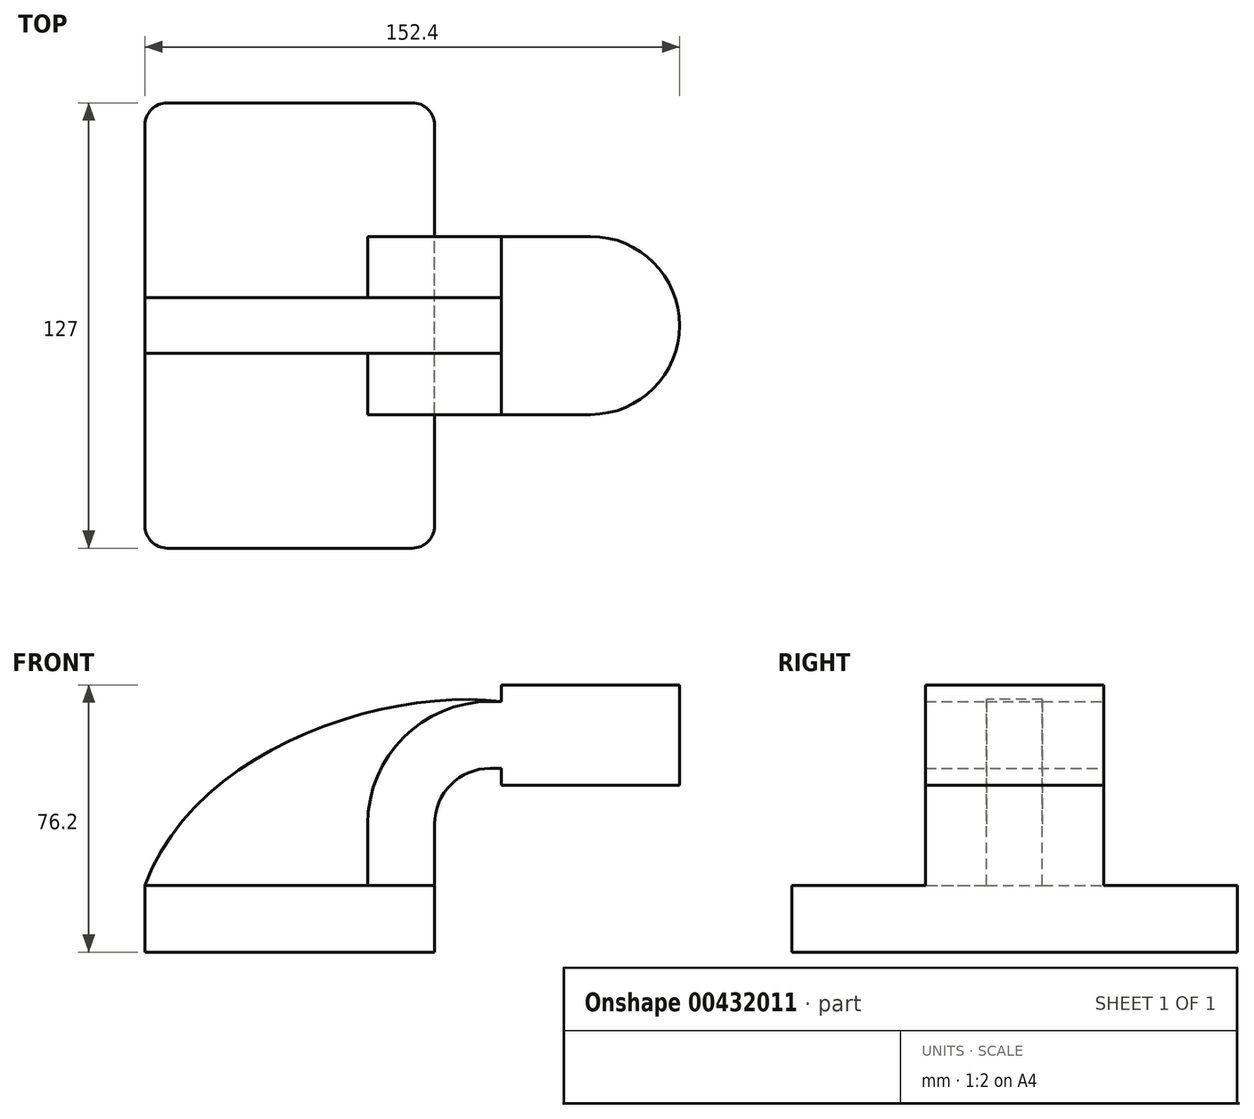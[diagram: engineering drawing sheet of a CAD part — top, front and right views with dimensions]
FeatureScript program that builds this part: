
annotation { "Feature Type Name" : "Feature", "Feature Type Description" : "" }
export const myFeature = defineFeature(function(context is Context, id is Id, definition is map)
    precondition{}
    {
        {
            var Q0;
            Q0=qCreatedBy(makeId("Front.planeOp"),FACE);
            var sketch = newSketch(context, id + "F0", { "sketchPlane" : qUnion([Q0])});
            skLineSegment(sketch, "E0.bottom", {"start": v(-41.28, -9.53) * mm, "end": v(41.28, -9.53) * mm});
            skLineSegment(sketch, "E0.top", {"start": v(-41.28, 9.53) * mm, "end": v(41.28, 9.53) * mm});
            skLineSegment(sketch, "E0.left", {"start": v(-41.28, -9.53) * mm, "end": v(-41.28, 9.53) * mm});
            skLineSegment(sketch, "E0.right", {"start": v(41.28, -9.53) * mm, "end": v(41.28, 9.53) * mm});
            skPoint(sketch, "E0.middle", {"position": v(0, 0) * mm});
            skLineSegment(sketch, "E1.bottom", {"start": v(111.12, 38.1) * mm, "end": v(60.32, 38.1) * mm});
            skLineSegment(sketch, "E1.top", {"start": v(111.13, 66.67) * mm, "end": v(60.33, 66.67) * mm});
            skLineSegment(sketch, "E1.left", {"start": v(111.13, 38.1) * mm, "end": v(111.13, 66.67) * mm});
            skLineSegment(sketch, "E1.right", {"start": v(60.33, 38.1) * mm, "end": v(60.33, 66.68) * mm});
            skPoint(sketch, "E1.middle", {"position": v(85.73, 52.39) * mm});
            skLineSegment(sketch, "E2", {"start": v(41.28, 9.52) * mm, "end": v(41.28, 27) * mm});
            skArc(sketch, "E3", {"start": v(41.27, 27) * mm, "mid": v(45.92, 38.23) * mm, "end": v(57.15, 42.88) * mm});
            skLineSegment(sketch, "E4", {"start": v(57.15, 42.88) * mm, "end": v(60.33, 42.88) * mm});
            skLineSegment(sketch, "E5.0", {"start": v(57.15, 61.93) * mm, "end": v(60.33, 61.93) * mm});
            skArc(sketch, "E5.1", {"start": v(22.23, 27) * mm, "mid": v(32.45, 51.7) * mm, "end": v(57.15, 61.93) * mm});
            skLineSegment(sketch, "E5.2", {"start": v(22.22, 9.52) * mm, "end": v(22.22, 27) * mm});
            skLineSegment(sketch, "E6", {"start": v(85.72, 38.1) * mm, "end": v(85.73, 66.67) * mm});
            skFitSpline(sketch, "E7", {"points": [v(-41.28, 9.53) * mm, v(60.33, 61.93) * mm], "startDerivative": vector(42.58, 116.43) * mm, "endDerivative": vector(100.86, -12.26) * mm});
            skSolve(sketch);
        }
        {
            var Q0;
            Q0=makeQuery(id+"F0.imprint","IMPRINT",FACE,{"disambiguationData":[TD([[makeQuery(id+"F0.imprint","IMPRINT",EDGE,{"derivedFrom":sQuery(id+"F0.wireOp",EDGE,"E0.bottom")}),1.0]])]});
            extrude(context, id + "F1", {"entities" : qUnion([Q0]), "endBound" : BoundingType.SYMMETRIC, "depth" : 127 * mm});
        }
        {
            var Q0;
            {var subQ0=sQuery(id+"F0.wireOp",EDGE,"E2");Q0=makeQuery(id+"F0.imprint","IMPRINT",FACE,{"disambiguationData":[TD([[makeQuery(id+"F0.imprint","IMPRINT",EDGE,{"derivedFrom":subQ0}),1.0]])]});}
            var Q1;
            {var subQ6=sQuery(id+"F0.wireOp",EDGE,"E6");Q1=makeQuery(id+"F0.imprint","IMPRINT",FACE,{"disambiguationData":[TD([[makeQuery(id+"F0.imprint","IMPRINT",EDGE,{"derivedFrom":subQ6}),1.0]])]});}
            extrude(context, id + "F2", {"entities" : qUnion([Q0, Q1]), "operationType" : NewBodyOperationType.ADD, "endBound" : BoundingType.SYMMETRIC, "depth" : 50.8 * mm});
        }
        {
            var Q0;
            Q0=makeQuery(id+"F0.imprint","IMPRINT",FACE,{"disambiguationData":[TD([[makeQuery(id+"F0.imprint","IMPRINT",EDGE,{"derivedFrom":sQuery(id+"F0.wireOp",EDGE,"E5.0")}),1.0]])]});
            extrude(context, id + "F3", {"entities" : qUnion([Q0]), "operationType" : NewBodyOperationType.ADD, "endBound" : BoundingType.SYMMETRIC, "depth" : 15.88 * mm});
        }
        {
            var Q0;
            {var subQ0=sQuery(id+"F0.wireOp",EDGE,"E1.left");Q0=makeQuery(id+"F0.imprint","IMPRINT",FACE,{"disambiguationData":[TD([[makeQuery(id+"F0.imprint","IMPRINT",EDGE,{"derivedFrom":subQ0}),1.0]])]});}
            var Q1;
            Q1=sQuery(id+"F0.wireOp",EDGE,"E6");
            revolve(context, id + "F4", {"operationType" : NewBodyOperationType.ADD, "entities" : qUnion([Q0]), "axis" : qUnion([Q1]), "revolveType" : RevolveType.FULL});
        }
        {
            var Q0;
            Q0=makeQuery(id+"F1.opExtrude","CAP_EDGE",EDGE,{"disambiguationData":[OSD([sQuery(id+"F0.wireOp",EDGE,"E0.left")])],"isStart":false});
            var Q1;
            Q1=makeQuery(id+"F1.opExtrude","CAP_EDGE",EDGE,{"disambiguationData":[OSD([sQuery(id+"F0.wireOp",EDGE,"E0.right")])],"isStart":false});
            var Q2;
            Q2=makeQuery(id+"F1.opExtrude","CAP_EDGE",EDGE,{"disambiguationData":[OSD([sQuery(id+"F0.wireOp",EDGE,"E0.right")])],"isStart":true});
            var Q3;
            Q3=makeQuery(id+"F1.opExtrude","CAP_EDGE",EDGE,{"disambiguationData":[OSD([sQuery(id+"F0.wireOp",EDGE,"E0.left")])],"isStart":true});
            fillet(context, id + "F5", {"entities" : qUnion([Q0, Q1, Q2, Q3]), "radius" : 6.35 * mm, "tangentPropagation" : true, "allowEdgeOverflow" : false});
        }
    });
